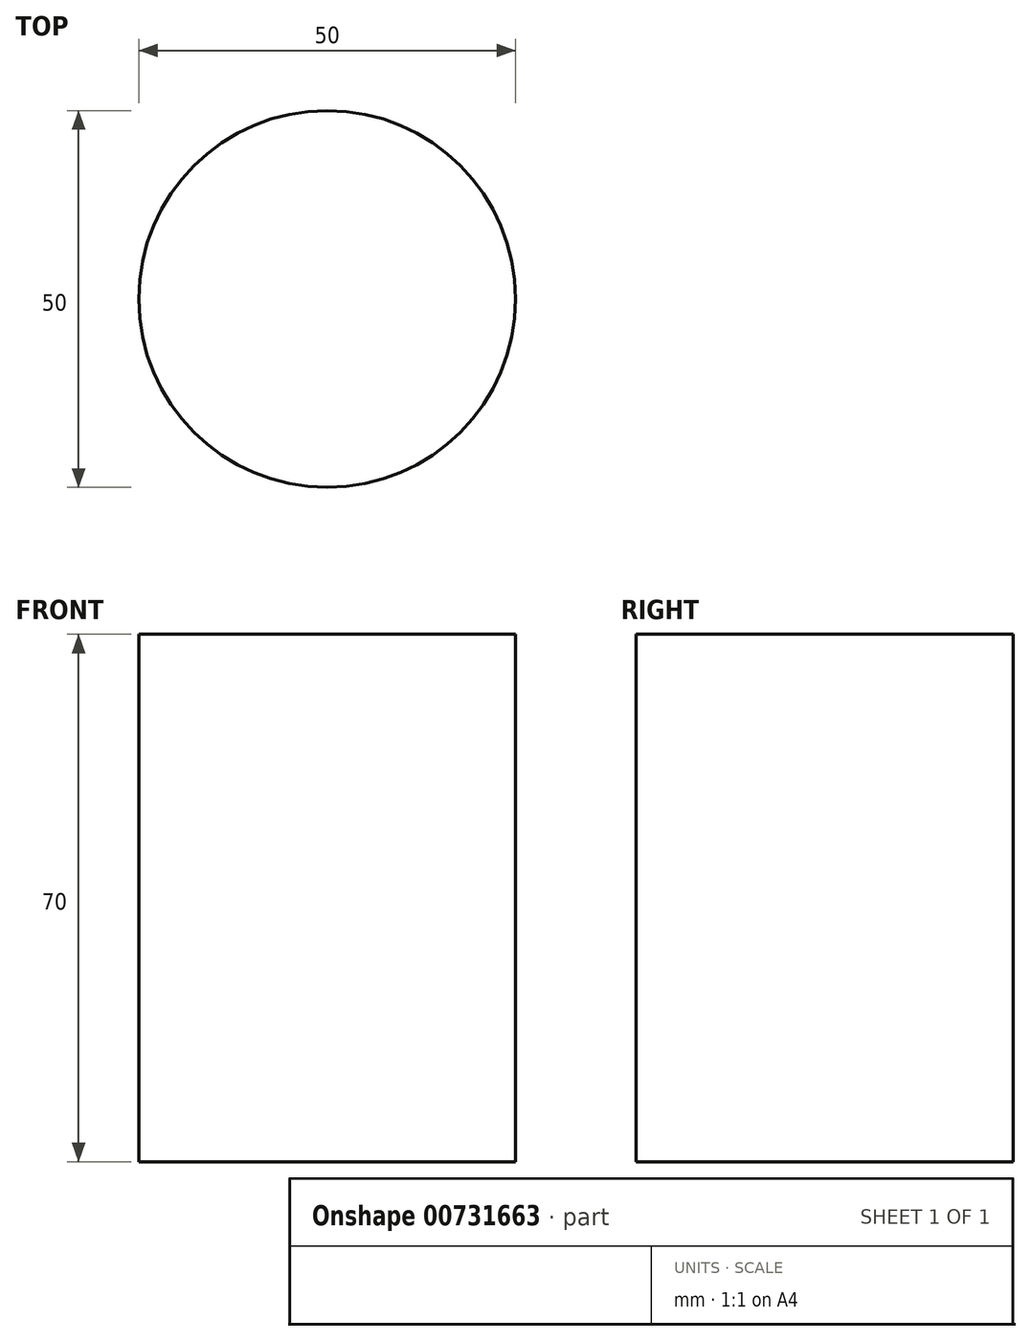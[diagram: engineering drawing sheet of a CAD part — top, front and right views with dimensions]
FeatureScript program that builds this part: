
annotation { "Feature Type Name" : "Feature", "Feature Type Description" : "" }
export const myFeature = defineFeature(function(context is Context, id is Id, definition is map)
    precondition{}
    {
        {
            var Q0;
            Q0=qCreatedBy(makeId("Top.planeOp"),FACE);
            var sketch = newSketch(context, id + "F0", { "sketchPlane" : qUnion([Q0])});
            skCircle(sketch, "E0", {"center": v(0, 0) * mm, "radius": 25 * mm});
            skSolve(sketch);
        }
        {
            var Q0;
            Q0=makeQuery(id+"F0.imprint","IMPRINT",FACE,{"disambiguationData":[TD([[makeQuery(id+"F0.imprint","IMPRINT",EDGE,{"derivedFrom":sQuery(id+"F0.wireOp",EDGE,"E0")}),1.0]])]});
            extrude(context, id + "F1", {"entities" : qUnion([Q0]), "depth" : 70 * mm, "offsetDistance" : 25 * mm});
        }
    });
